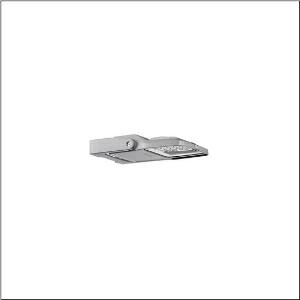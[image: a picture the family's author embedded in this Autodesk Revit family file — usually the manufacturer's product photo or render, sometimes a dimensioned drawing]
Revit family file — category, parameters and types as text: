
# Revit family: floodlight_fl_21_iq_micro___pl33t_5xa7761a2f2a_98c0
name_source: partatom
category: Lighting Fixtures
units: mm (PartAtom-declared; Revit-internal decimal feet)

## family parameters
Cut with Voids When Loaded = No
Host = Face
Light Source = No
Part Type = Normal
Room Calculation Point = No
Round Connector Dimension = Use Diameter
Shared = No

## types (1)
- --- (1 x LED, 2930 lm, 23.1 W, 3000K)
    Apparent Load = 23 VA
    CIE Flux Codes = 26 75 99 100 100
    Color Rendering = 70
    Color Temperature = 3000K
    Default Elevation = 1800 mm
    Description = Floodlight FL 21 iQ micro, floodlight, primary light control with lens, of PMMA, primary optical cover: protective disc, of toughened safety glass, transparent, light distribution: PL33T, light emission: direct distribution, installation type: surface-mounted, LED, High Power LED, rated luminous flux: 2.930lm, luminous efficacy: 127lm/W, light colour: 730, colour temperature: 3000K, control: optimised constant luminous flux control (CLO 2.0), Desk-Remote (wireless, voltage-free reading and setting of iQ features in the workshop via application-optimized NFC function/RFID function), Light-Fading, Smart-Wire, Night-Set, Lumen-Switch, Temp-Guard, Auto-Match, with terminal, 6-pole, mains connection: 220..240V, AC, 50/60Hz, start of lifetime: 23W, end of service life: 24W, reduction: 11W, luminaire housing, of diecast aluminium, powder-coated, Siteco® metallic grey (DB 702S), corrosivity category C5 mid according to DIN EN ISO 12944, sealing non-destructively replaceable, design bracket, of diecast aluminium, powder-coated, Siteco® metallic grey (DB 702S), protection rating (complete): IP66, insulation class (complete): insulation class II (safety insulation), certification: CE, ENEC, VDE, protection symbol: D, impact resistance: IK07, permissible operating ambient temperature: -40..+40°C, permissible operating ambient temperature for outdoor applications: -40..+50°C, standard: DIN EN 12944, LABS conformity tested according to VDMA 24364:2018-05, packaging unit: 1 piece

Light Distribution: PL33T
    Height = 65 mm
    Lamp = 1 x LED
    Lamp Light Flux = 2930 lm
    Lamp Power = 23.1 W
    Lamp count = 1
    Length = 312 mm
    Luminous efficacy = 127 lm/W
    Manufacturer = Siteco
    ModVariant = No
    Model = 5XA7761A2F2A
    Mounting Place = Wall
    Mounting Type = Surface mounted
    Number of Poles = 1
    OnlyDefault = Yes
    Power Factor = 1
    Product Name = Floodlight FL 21 iQ micro | PL33T
    Product group = floodlight | wall mounted
    ProductGroupID = 2001
    Protection Class = Protection class II
    Protection Degree = IP 66
    RLX_Detail_Level = 1
    RLX_Emergency_Light_Flux = 0 lm
    RLX_Emergency_Type = 0
    RLX_Emergency_Type_DB = No
    RlxData = <blob elided: 97145 chars, md5=b817bda2>
    Socket = socket
    Standby Power = 0 W
    System Light Flux = 2930 lm
    System Power = 23 W
    Type Comments = factory setting: luminous flux: 100 % | dim-lin: 254 | 455 mA
    Type Image = l_1006878.jpg
    URL = http://relux.com
    VarID = @adj_118595
    Voltage = 0 V
    Weight = 0.00 kg
    Width = 230 mm

## geometry (parser evidence)
native form markers: Blend x4, Sweep x12
no freeform markers — native parametric forms only
